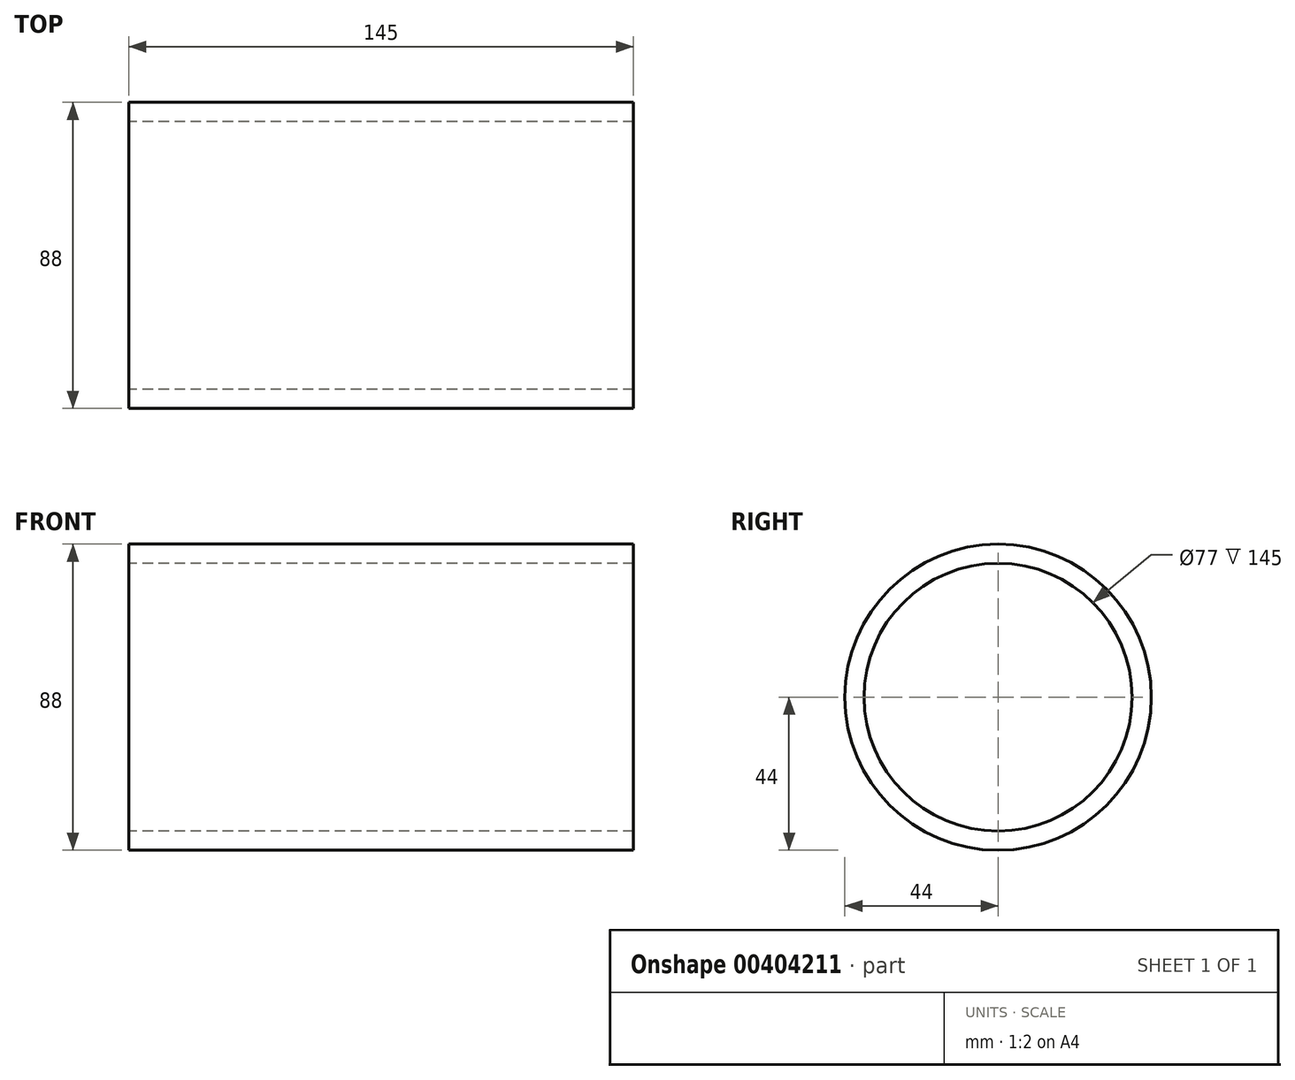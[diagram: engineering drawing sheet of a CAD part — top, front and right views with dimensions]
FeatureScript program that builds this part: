
annotation { "Feature Type Name" : "Feature", "Feature Type Description" : "" }
export const myFeature = defineFeature(function(context is Context, id is Id, definition is map)
    precondition{}
    {
        {
            var Q0;
            Q0=qCreatedBy(makeId("Right.planeOp"),FACE);
            var sketch = newSketch(context, id + "F0", { "sketchPlane" : qUnion([Q0])});
            skCircle(sketch, "E0", {"center": v(0, 0) * mm, "radius": 38.5 * mm});
            skCircle(sketch, "E1", {"center": v(0, 0) * mm, "radius": 44 * mm});
            skSolve(sketch);
        }
        {
            var Q0;
            Q0 = qSketchRegion(id + "F0", true);
            extrude(context, id + "F1", {"entities" : qUnion([Q0]), "endBound" : BoundingType.SYMMETRIC, "depth" : 145 * mm});
        }
    });
